# Revit family: EL_Hassta_v2
name_source: partatom
category: Lighting Fixtures
units: mm (PartAtom-declared; Revit-internal decimal feet)

## family parameters
Always vertical = Yes
Cut with Voids When Loaded = No
Light Source = Yes
Maintain Annotation Orientation = No
OmniClass Number = 23.80.70.00
OmniClass Title = Lighting
Part Type = Normal
Room Calculation Point = No
Round Connector Dimension = Use Diameter
Shared = No
Work Plane-Based = No

## types (37) — shared parameters
CCT = 4000
CE Conformity = CE Mark
CRI = 70
Certification = ENEC, ENEC+, EMC, Zhaga D4i, IDA
Color Filter = 16777215
Control Gear = LED Driver
Default Elevation = 4155 mm  [stored 13.6319 ft]
Description = Street luminaire
Diffuser Material  = Flat glass
Dimming Lamp Color Temperature Shift = <None>
EL_Voltage = AC 220V - 240V / 50-60Hz
Emit from Line Length = 610 mm
Housing Height = 191 mm  [stored 0.62664 ft]
Housing Length = 696 mm  [stored 2.28346 ft]
Housing Width = 248 mm  [stored 0.813648 ft]
IK = IK 08
IP = IP66
Lamp = LED
Life Time = 120 000 h
Light Source Symbol Length = 3048 mm  [stored 10 ft]
Luminaire Material = <By Category>
Luminaire Model = HASSTA 2  Mxx 9k0 740
Luminaire Type = HASSTA 2
Luminous Flux of LED = 9000 lm
Luminous Flux of Luminaire = 7095 lm
Manufacturer = ELEKTRO-LUMEN, s. r. o.
Model = HASSTA 2
Optic = M03
Optical Efficacy = 78.83
Power = 52 W
Spot Beam Angle = 30.00°
Spot Field Angle = 90.00°
Terminal Block Poles = 2, 3, 5
Tilt Angle = 90.00°
URL Luminaire = https://www.el-lumen.cz
URL Manufacturer = https://www.el-lumen.cz
Voltage  = AC 220V - 240V / 50-60Hz
Weight = 8

## type names (no varying parameters)
- HASSTA 2Lxx 2k0 AMB
- HASSTA 2Lxx 3k0 AMB
- HASSTA 2Lxx 4k0 AMB
- HASSTA 2Lxx 5k0 AMB
- HASSTA 2Lxx 6k0 AMB
- HASSTA 2Lxx 7k0 AMB
- HASSTA 2Lxx 8k0 AMB
- HASSTA 2Mxx 2k0 722
- HASSTA 2Mxx 3k0 722
- HASSTA 2Mxx 4k0 722
- HASSTA 2Mxx 5k0 722
- HASSTA 2Mxx 6k0 722
- HASSTA 2Mxx 7k0 722
- HASSTA 2Mxx 2k0 727
- HASSTA 2Mxx 3k0 727
- HASSTA 2Mxx 4k0 727
- HASSTA 2Mxx 5k0 727
- HASSTA 2Mxx 6k0 727
- HASSTA 2Mxx 7k0 727
- HASSTA 2Mxx 8k0 727
- HASSTA 2Mxx 9k0 727
- HASSTA 2Mxx 2k0 730
- HASSTA 2Mxx 3k0 730
- HASSTA 2Mxx 4k0 730
- HASSTA 2Mxx 5k0 730
- HASSTA 2Mxx 6k0 730
- HASSTA 2Mxx 7k5 730
- HASSTA 2Mxx 8k0 730
- HASSTA 2Mxx 9k0 730
- HASSTA 2Mxx 2k0 740
- HASSTA 2Mxx 3k0 740
- HASSTA 2Mxx 4k0 740
- HASSTA 2Mxx 5k0 740
- HASSTA 2Mxx 6k0 740
- HASSTA 2Mxx 7k0 740
- HASSTA 2Mxx 8k0 740
- HASSTA 2Mxx 9k0 740

note: [stored X ft] marks values corroborated as IEEE doubles in the binary element streams (Revit-internal decimal feet)
